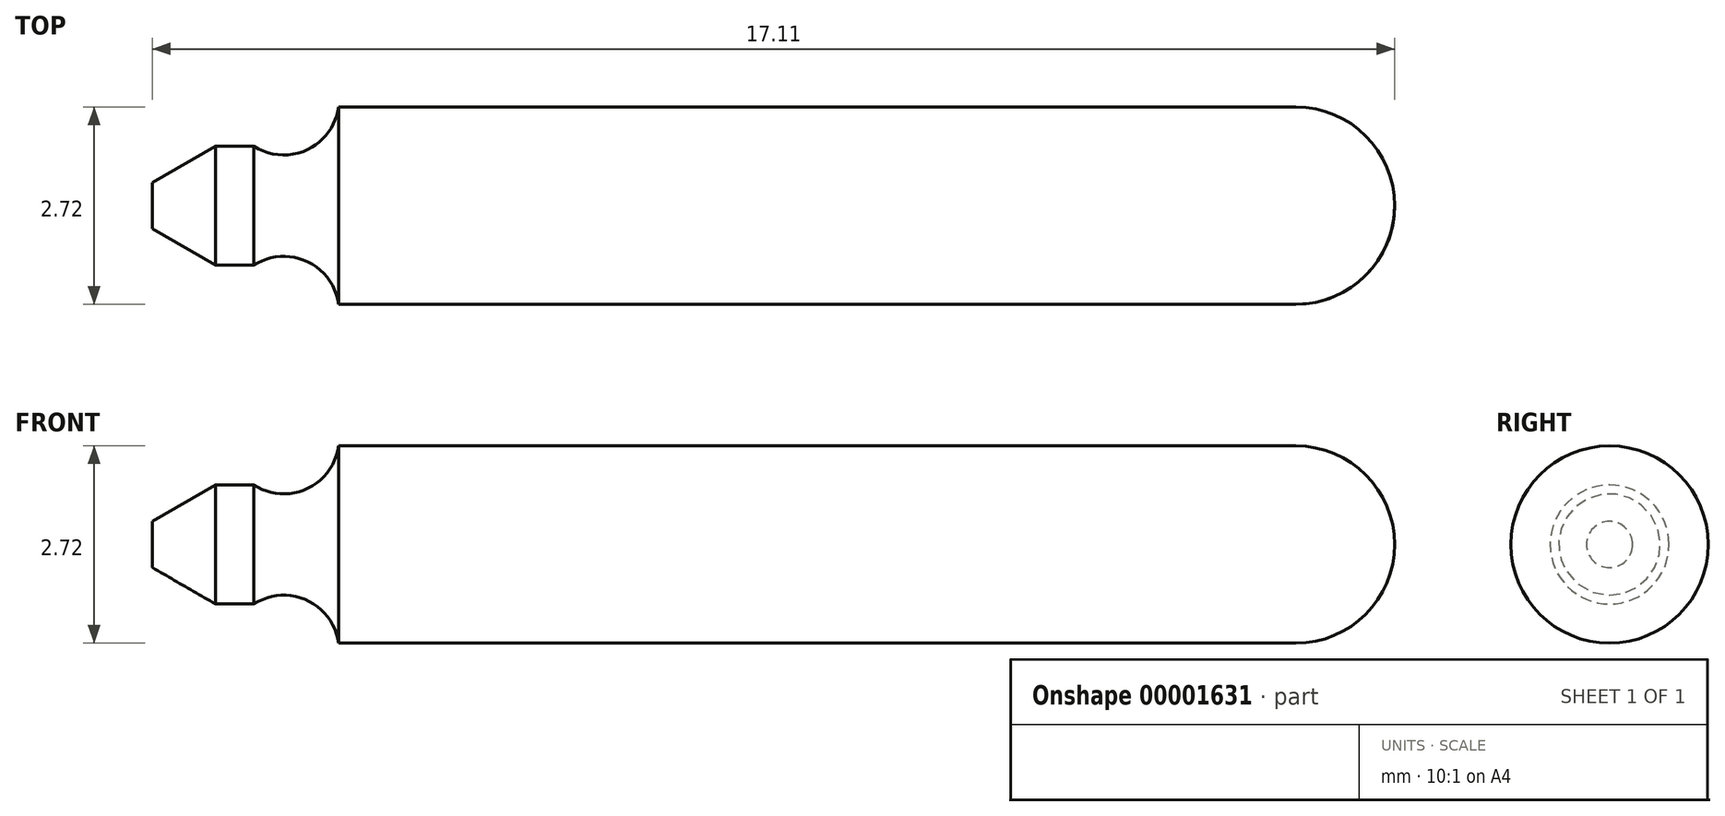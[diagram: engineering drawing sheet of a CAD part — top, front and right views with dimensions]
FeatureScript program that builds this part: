
annotation { "Feature Type Name" : "Feature", "Feature Type Description" : "" }
export const myFeature = defineFeature(function(context is Context, id is Id, definition is map)
    precondition{}
    {
        {
            var Q0;
            Q0=qCreatedBy(makeId("Top.planeOp"),FACE);
            var sketch = newSketch(context, id + "F0", { "sketchPlane" : qUnion([Q0])});
            skLineSegment(sketch, "E0", {"start": v(0, 0) * mm, "end": v(-13.18, 0) * mm});
            skLineSegment(sketch, "E1", {"start": v(0, 1.36) * mm, "end": v(-15.75, 1.36) * mm});
            skArc(sketch, "E2", {"start": v(-13.18, 0) * mm, "mid": v(-13.62, 0.59) * mm, "end": v(-14.35, 0.54) * mm});
            skLineSegment(sketch, "E3", {"start": v(-14.35, 0.54) * mm, "end": v(-14.88, 0.54) * mm});
            skLineSegment(sketch, "E4", {"start": v(-14.88, 0.54) * mm, "end": v(-15.75, 1.04) * mm});
            skLineSegment(sketch, "E5", {"start": v(-15.75, 1.04) * mm, "end": v(-15.75, 1.36) * mm});
            skArc(sketch, "E6", {"start": v(0, 0) * mm, "mid": v(0.96, 0.4) * mm, "end": v(1.36, 1.36) * mm});
            skLineSegment(sketch, "E7", {"start": v(0, 1.36) * mm, "end": v(1.36, 1.36) * mm});
            skSolve(sketch);
        }
        {
            var Q0;
            Q0=makeQuery(id+"F0.imprint","IMPRINT",FACE,{"disambiguationData":[TD([[makeQuery(id+"F0.imprint","IMPRINT",EDGE,{"derivedFrom":sQuery(id+"F0.wireOp",EDGE,"E0")}),-1.0]])]});
            var Q1;
            Q1=sQuery(id+"F0.wireOp",EDGE,"E1");
            revolve(context, id + "F1", {"entities" : qUnion([Q0]), "axis" : qUnion([Q1]), "revolveType" : RevolveType.FULL});
        }
    });
